# Revit family: agtatec_Record_SldngDrset_CLEAN-K1_WallBased_Glass
name_source: partatom
category: Doors
revit_build: Autodesk Revit Architecture 2014 (Build: 20130308_1515(x64)
units: mm (PartAtom-declared; Revit-internal decimal feet)

## types (2) — shared parameters
AccessoryOptions = contact manufacturer
AlternativeDoorsetGlazing = Noise protection, radiation protection, smoke- and fire protection
AntiFingerTrapRequirement = No
Assembly Code = B2030300
BIMObjectName = agtatec_Record_SlidingDoorset_CLEAN-K1_WallBased
BreakoutFacility = 0
ClearanceZones = No
Colour = customer specific
Configuration = 1
Construction Type = Automatic Sliding Door
Description = Automatic Sliding Door
DoorIncluded = Yes
DoorSeal = rubber
DoorsetFasteners = screws
DoorsetOperation = automatic, manual
DurationUnit = year
ElectronicLock = No
Finish = Powder coated, Anodized, customer specific
FireExit = No
FrameColourOptions = all RAL, customer specific
FrameFinish = part of glazing spec
FrameFinishOptions = Powder coated, Anodized, Clad in stainless steel, etc.
FrameMaterial = aluminum, stainless steel, HPL
FrameProfile = aluminum
FrameSeal = Yes
Function = Exterior
GlassLayers = 1
GlassThickness1 = 0
GlassThickness2 = 0
GlassType = customer specific
HandicapAccessible = Yes
HasDrive = Yes
IfcExportAs = IfcDoorStyle
IfcExportType = Door
IsExternal = No
IssueDate = (leave empty)
LeafColourOptions = customer specific
ManufacturerURL = www.kos-tueren.de
Material = wood, stainless steel, aluminum, HPL
Model = record CLEAN basic linear slider single leaf
ModelReference = depends on the configuration
NBSDescription = Sliding Doorset
Name = SldngDrset_CLEAN-K1_WallBased_Record
OpenDoor = No
OpeningMechanism = automatic, manual
OperatingTemperature = -15° to +50°C
Operation = Automatic
PanelFill = agtatec_Record_White
PanelGlass = agtatec_Record_Glass
PassageWidthOptions = Depends on diameter, Opening Angle is 69.4° (-70 mm)
ProductInformation = www.agta-record.com
ReferenceStandard = EN16005, DIN 18650, etc.
ReplacementCost = depends on the configuration and door type
Rubber = agtatec_Record_Rubber
SafetyDevices = Fully compliant with EN16005, Safety buffers, Presence sensors, etc.
SelfClosing = Yes
ServiceLifeDuration = 10-15 years
Shape = rectangular
SideStrip = Yes
SideStripWidth = 150 mm
SmokeStop = No
ThresholdRequired = Yes
URL = www.agta-record.com
Uniclass2 = Ss_25_30_20_77
Version = Version 1.0
WarrantyDescription = Depends on country
WarrantyDurationLabour = Depends on country
WarrantyDurationParts = Depends on country
WarrantyDurationUnit = Blank value needs populating
WarrantyGuarantorLabour = Local door manufacturer
WarrantyGuarantorParts = Local door manufacturer
Weight = Depends on configuration and size
Window = Yes
WithinStandardSizes = Yes
zero-valued in all types: Cost, NominalHeight, NominalLength, NominalWidth, OffsetFromWallSide, OffsetFromWallTop, ThermalTransmittance, Thickness

## per-type parameters (varying)
| type | DimensionUnfinished | Frames | FreePassage | Handle | Handles | Height | HeightCentreFlushMountedSocket | HeightOfUnfinishedState | HeightToTopOfTravellingMechanismCovering | InsideFrameHeight | InsideFrameWidth | OpeningHeight | OpeningWidth | PanelWidth | Rough Height | Rough Width | Sensor | SideStripMaterial | TravellingMechanismCoveringWidth | Width | WindowHeight | WindowSillHeight | WindowWidth |
| CLEAN K1 | 1240 mm | agtatec_Record_Aluminium | 1075 mm | agtatec_Record_Aluminium | Yes | 2405 mm  [stored 7.89042 ft] | 2325 mm | 2125 mm | 2405 mm  [stored 7.89042 ft] | 2100 mm | 1200 mm | 2100 mm | 1200 mm | 1260 mm  [stored 4.13386 ft] | 2470 mm  [stored 8.10367 ft] | 2455 mm  [stored 8.05446 ft] | agtatec_Record_Aluminium | agtatec_Record_Aluminium | 2455 mm  [stored 8.05446 ft] | 2455 mm  [stored 8.05446 ft] | 600 mm | 1200 mm | 600 mm |
| Clean K1 Glass | 1440 mm | agtatec_Record_StainlessSteel | 1275 mm  [stored 4.18307 ft] | agtatec_Record_StainlessSteel | No | 2605 mm  [stored 8.54659 ft] | 2525 mm  [stored 8.28412 ft] | 2325 mm | 2605 mm  [stored 8.54659 ft] | 2300 mm | 1400 mm  [stored 4.59318 ft] | 2300 mm | 1400 mm  [stored 4.59318 ft] | 1460 mm  [stored 4.79003 ft] | 2670 mm  [stored 8.75984 ft] | 2855 mm  [stored 9.3668 ft] | agtatec_Record_StainlessSteel | agtatec_Record_StainlessSteel | 2855 mm  [stored 9.3668 ft] | 2855 mm  [stored 9.3668 ft] | 2170 mm  [stored 7.11942 ft] | 120 mm  [stored 0.393701 ft] | 1220 mm  [stored 4.00262 ft] |

note: [stored X ft] marks values corroborated as IEEE doubles in the binary element streams (Revit-internal decimal feet)

## geometry (parser evidence)
native form markers: Blend x2, Sweep x9
no freeform markers — native parametric forms only
